# Revit family: Legalett_L-Element_Hörn_Linatex_FOT-XPS300
name_source: partatom
category: Structural Foundations
units: mm (PartAtom-declared; Revit-internal decimal feet)

## family parameters
Always vertical = Yes
Cap = No
Cut with Voids When Loaded = No
Material for Model Behavior = Other
OmniClass Number = 23.25.05.00
OmniClass Title = Foundations
Shared = No
Show family pre-cut in plan views = Yes
Work Plane-Based = No

## types (4) — shared parameters
Length = 585 mm  [stored 1.91929 ft]
Manufacturer = Legalett
Structural Material = Default
Thickness = 100 mm  [stored 0.328084 ft]
Width = 585 mm  [stored 1.91929 ft]

## per-type parameters (varying)
| type | Foundation Thickness | Model | Type Comments |
| L300 Linatex XPS300 | 300 mm | Hörn L300 Linatex XPS300 | 21350-300H |
| L400 Linatex XPS300 | 400 mm  [stored 1.31234 ft] | Hörn L400 Linatex XPS300 | 21350-400H |
| L450 Linatex XPS300 | 450 mm  [stored 1.47638 ft] | Hörn L450 Linatex XPS300 | 21350-450H |
| L500 Linatex XPS300 | 500 mm  [stored 1.64042 ft] | Hörn L500 Linatex XPS300 | 21350-500H |

note: [stored X ft] marks values corroborated as IEEE doubles in the binary element streams (Revit-internal decimal feet)

## geometry (parser evidence)
native form markers: Blend x4, Sweep x4
no freeform markers — native parametric forms only
